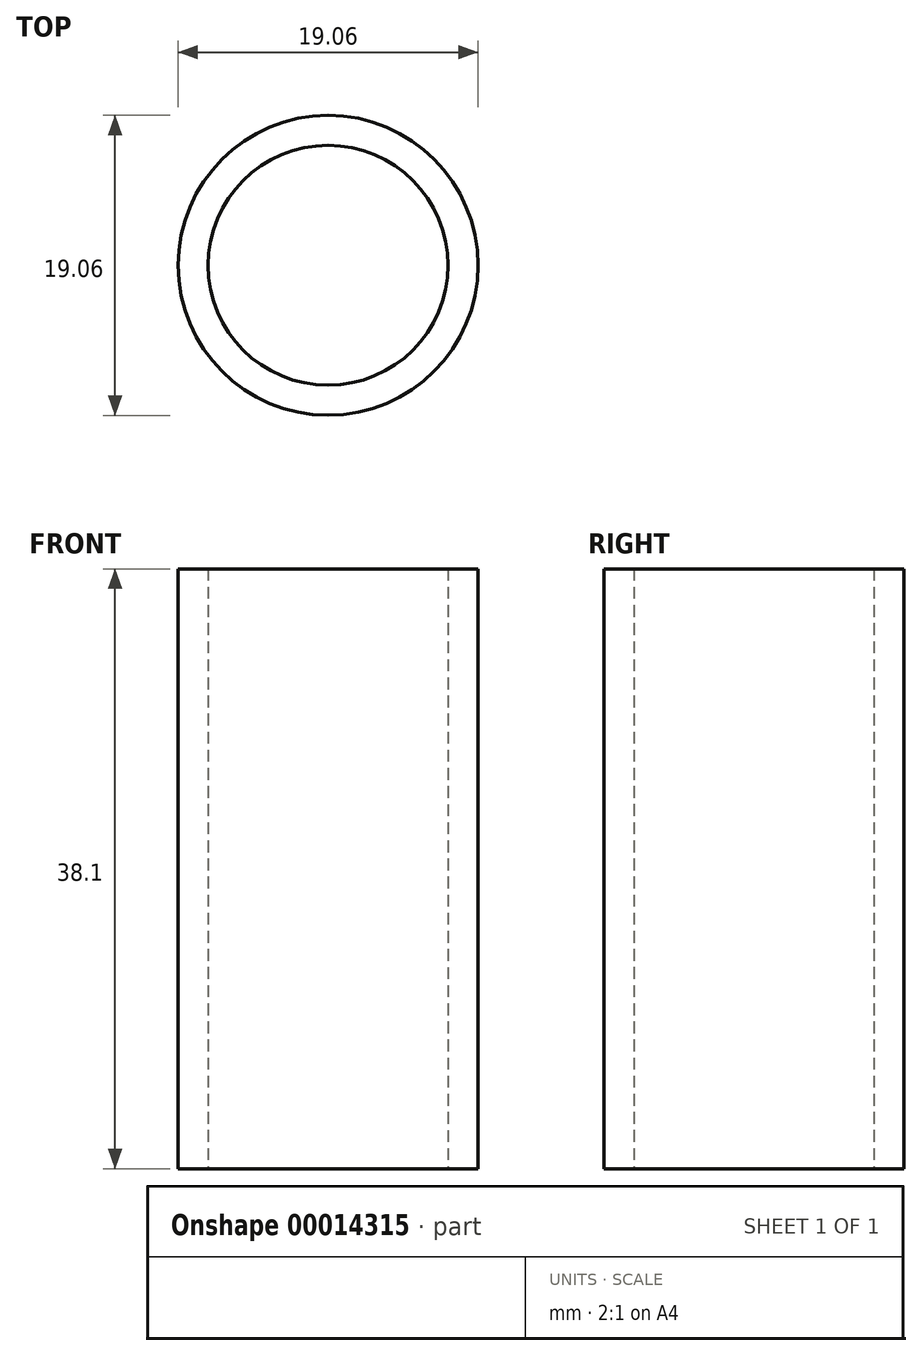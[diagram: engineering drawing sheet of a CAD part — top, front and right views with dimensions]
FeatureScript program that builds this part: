
annotation { "Feature Type Name" : "Feature", "Feature Type Description" : "" }
export const myFeature = defineFeature(function(context is Context, id is Id, definition is map)
    precondition{}
    {
        {
            var Q0;
            Q0=qCreatedBy(makeId("Top.planeOp"),FACE);
            var sketch = newSketch(context, id + "F0", { "sketchPlane" : qUnion([Q0])});
            skCircle(sketch, "E0", {"center": v(0, 0) * mm, "radius": 7.62 * mm});
            skCircle(sketch, "E1", {"center": v(0, 0) * mm, "radius": 9.53 * mm});
            skSolve(sketch);
        }
        {
            var Q0;
            Q0=qSketchRegion(id+"F0",true);
            extrude(context, id + "F1", {"entities" : qUnion([Q0]), "depth" : 38.1 * mm});
        }
    });
